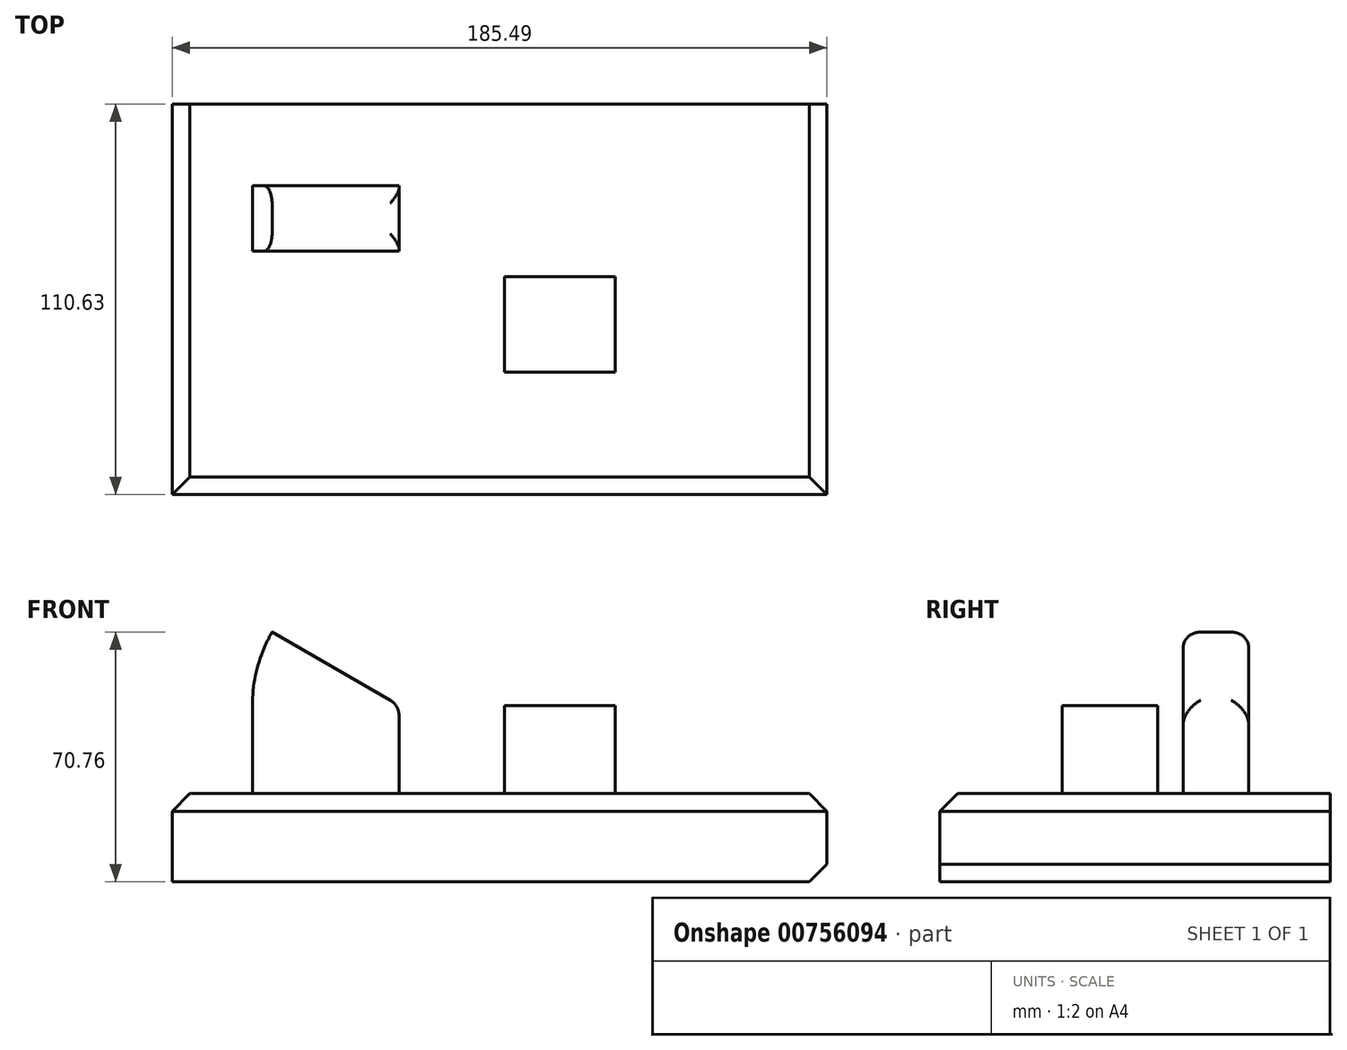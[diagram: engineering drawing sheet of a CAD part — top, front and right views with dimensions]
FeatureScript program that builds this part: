
annotation { "Feature Type Name" : "Feature", "Feature Type Description" : "" }
export const myFeature = defineFeature(function(context is Context, id is Id, definition is map)
    precondition{}
    {
        {
            var Q0;
            Q0=qCreatedBy(makeId("Top.planeOp"),FACE);
            var sketch = newSketch(context, id + "F0", { "sketchPlane" : qUnion([Q0])});
            skLineSegment(sketch, "E0.bottom", {"start": v(-34.81, -34.7) * mm, "end": v(150.68, -34.7) * mm});
            skLineSegment(sketch, "E0.top", {"start": v(-34.81, 75.94) * mm, "end": v(150.68, 75.94) * mm});
            skLineSegment(sketch, "E0.left", {"start": v(-34.81, -34.7) * mm, "end": v(-34.81, 75.94) * mm});
            skLineSegment(sketch, "E0.right", {"start": v(150.68, -34.7) * mm, "end": v(150.68, 75.94) * mm});
            skSolve(sketch);
        }
        {
            var Q0;
            Q0 = qSketchRegion(id + "F0", true);
            extrude(context, id + "F1", {"entities" : qUnion([Q0]), "depth" : 25 * mm, "offsetDistance" : 25 * mm});
        }
        {
            var Q0;
            Q0=makeQuery(id+"F1.opExtrude","CAP_EDGE",EDGE,{"disambiguationData":[OSD([sQuery(id+"F0.wireOp",EDGE,"E0.bottom")])],"isStart":false});
            var Q1;
            Q1=makeQuery(id+"F1.opExtrude","CAP_EDGE",EDGE,{"disambiguationData":[OSD([sQuery(id+"F0.wireOp",EDGE,"E0.left")])],"isStart":false});
            var Q2;
            Q2=makeQuery(id+"F1.opExtrude","CAP_EDGE",EDGE,{"disambiguationData":[OSD([sQuery(id+"F0.wireOp",EDGE,"E0.right")])],"isStart":false});
            var Q3;
            Q3=makeQuery(id+"F1.opExtrude","CAP_EDGE",EDGE,{"disambiguationData":[OSD([sQuery(id+"F0.wireOp",EDGE,"E0.right")])],"isStart":true});
            chamfer(context, id + "F2", {"entities" : qUnion([Q0, Q1, Q2, Q3]), "width" : 5 * mm, "tangentPropagation" : true});
        }
        {
            var Q0;
            Q0=makeQuery(id+"F1.opExtrude","CAP_FACE",FACE,{"disambiguationData":[OSD([sQuery(id+"F0.wireOp",EDGE,"E0.bottom"),sQuery(id+"F0.wireOp",EDGE,"E0.top"),sQuery(id+"F0.wireOp",EDGE,"E0.left"),sQuery(id+"F0.wireOp",EDGE,"E0.right")])],"isStart":false});
            var sketch = newSketch(context, id + "F3", { "sketchPlane" : qUnion([Q0])});
            skLineSegment(sketch, "E1.bottom", {"start": v(59.29, 0) * mm, "end": v(90.69, 0) * mm});
            skLineSegment(sketch, "E1.top", {"start": v(59.29, 27) * mm, "end": v(90.69, 27) * mm});
            skLineSegment(sketch, "E1.left", {"start": v(59.29, 0) * mm, "end": v(59.29, 27) * mm});
            skLineSegment(sketch, "E1.right", {"start": v(90.69, 0) * mm, "end": v(90.69, 27) * mm});
            skLineSegment(sketch, "E2.bottom", {"start": v(29.46, 34.22) * mm, "end": v(-12.07, 34.22) * mm});
            skLineSegment(sketch, "E2.top", {"start": v(29.46, 52.8) * mm, "end": v(-12.07, 52.8) * mm});
            skLineSegment(sketch, "E2.left", {"start": v(29.46, 34.22) * mm, "end": v(29.46, 52.8) * mm});
            skLineSegment(sketch, "E2.right", {"start": v(-12.07, 34.22) * mm, "end": v(-12.07, 52.8) * mm});
            skSolve(sketch);
        }
        {
            var Q0;
            Q0 = qSketchRegion(id + "F3", true);
            extrude(context, id + "F4", {"entities" : qUnion([Q0]), "operationType" : NewBodyOperationType.ADD, "depth" : 25 * mm, "offsetDistance" : 25 * mm});
        }
        {
            var Q0;
            Q0=makeQuery(id+"F4.opExtrude","CAP_FACE",FACE,{"disambiguationData":[OSD([sQuery(id+"F3.wireOp",EDGE,"E2.bottom"),sQuery(id+"F3.wireOp",EDGE,"E2.top"),sQuery(id+"F3.wireOp",EDGE,"E2.left"),sQuery(id+"F3.wireOp",EDGE,"E2.right")])],"isStart":false});
            var Q1;
            Q1=makeQuery(id+"F4.opExtrude","CAP_EDGE",EDGE,{"disambiguationData":[OSD([sQuery(id+"F3.wireOp",EDGE,"E2.left")])],"isStart":false});
            revolve(context, id + "F5", {"operationType" : NewBodyOperationType.ADD, "surfaceOperationType" : NewSurfaceOperationType.NEW, "entities" : qUnion([Q0]), "axis" : qUnion([Q1]), "revolveType" : RevolveType.ONE_DIRECTION, "angle" : 30 * degree});
        }
        {
            var Q0;
            Q0=makeQuery(id+"F5.opRevolve","CAP_EDGE",EDGE,{"disambiguationData":[OSD([sQuery(id+"F3.wireOp",EDGE,"E2.bottom")])],"isStart":false});
            var Q1;
            Q1=makeQuery(id+"F5.opRevolve","CAP_EDGE",EDGE,{"disambiguationData":[OSD([sQuery(id+"F3.wireOp",EDGE,"E2.top")])],"isStart":false});
            var Q2;
            {var subQ0=sQuery(id+"F3.wireOp",EDGE,"E2.left");Q2=makeQuery(id+"F5.boolean.opBoolean","MERGE",EDGE,{"derivedFrom":[makeQuery(id+"F4.opExtrude","CAP_EDGE",EDGE,{"disambiguationData":[OSD([subQ0])],"isStart":false}),makeQuery(id+"F5.opRevolve","CAP_EDGE",EDGE,{"disambiguationData":[OSD([subQ0])],"isStart":true})]});}
            fillet(context, id + "F6", {"entities" : qUnion([Q0, Q1, Q2]), "radius" : 5 * mm, "tangentPropagation" : true, "allowEdgeOverflow" : false});
        }
    });
